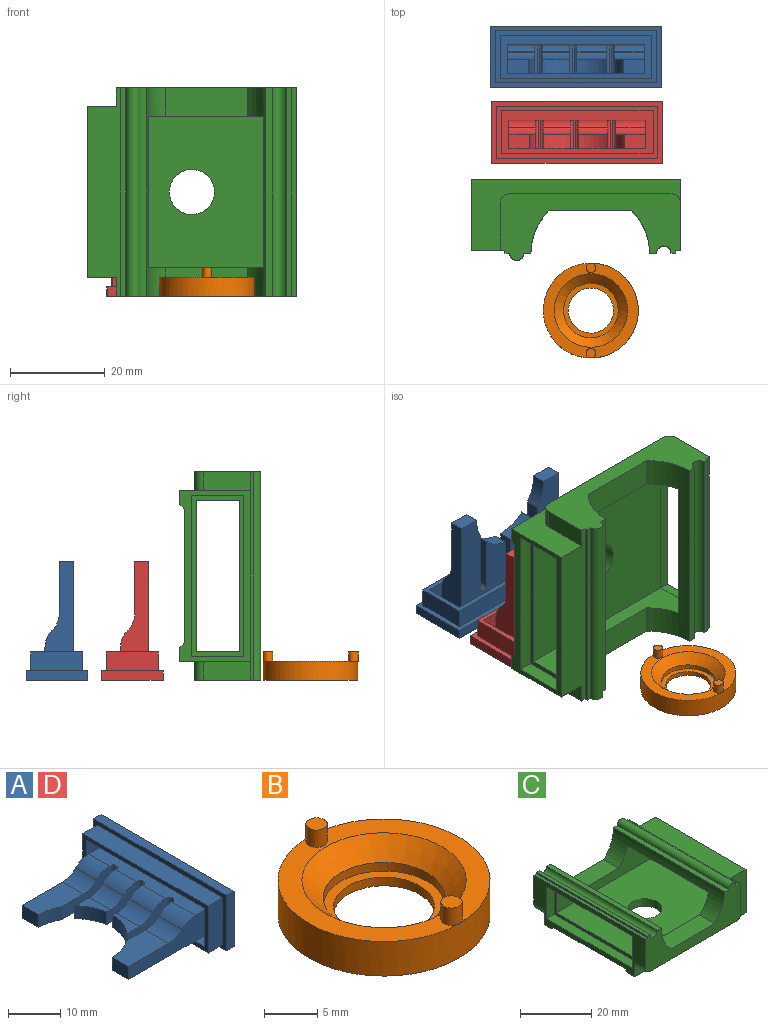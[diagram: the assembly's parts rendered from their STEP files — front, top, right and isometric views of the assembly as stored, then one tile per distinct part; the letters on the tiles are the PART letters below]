
ASSEMBLY  parts=4 mates=3
PART A: 57 faces, bbox 25x36x13 mm
  f0: plane 32x4mm, normal (0,0,-1), area 128mm2, adj f1,f7,f8,f24
  f1: plane 9x4mm, normal (0,-1,0), area 36mm2, adj f0,f2,f8,f24
  f2: plane 32x4mm, normal (0,0,1), area 128mm2, adj f1,f7,f8,f24
  f3: plane 11x4mm, normal (0,1,0), area 44mm2, adj f4,f6,f8,f41
  f4: plane 34x4mm, normal (0,0,1), area 136mm2, adj f3,f5,f8,f41
  f5: plane 11x4mm, normal (0,-1,0), area 44mm2, adj f4,f6,f8,f41
  f6: plane 34x4mm, normal (0,0,-1), area 136mm2, adj f3,f5,f8,f41
  f7: plane 9x4mm, normal (0,1,0), area 36mm2, adj f0,f2,f8,f24
  f8: plane 34x11mm, normal (-1,0,0), area 86mm2, adj f0,f1,f2,f3,f4,f5,f6,f7
  f9: plane 6x0.4mm, normal (-1,0,0), area 2.4mm2, adj f33,f37,f51,f52
  f10: plane 6x0.4mm, normal (-1,0,0), area 2.4mm2, adj f33,f37,f55,f56
  f11: plane 6x0.4mm, normal (-1,0,0), area 2.4mm2, adj f33,f37,f53,f54
  f12: cylinder r=5mm len=5.7mm, axis (0,-1,0), area 22.4mm2, adj f13,f33,f36,f38
  f13: plane 5.7x0.07mm, normal (-0.71,0,0.71), area 0.6mm2, adj f12,f36,f38,f47
  f14: cylinder r=10mm len=5.7mm, axis (0,0,-1), area 19.5mm2, adj f15,f32,f34,f37
  f15: plane 5.7x3.89mm, normal (0,0,1), area 11.8mm2, adj f14,f32,f34,f48
  f16: cylinder r=5mm len=6.3mm, axis (0,-1,0), area 24.7mm2, adj f17,f27,f28,f33
  f17: plane 6.3x0.07mm, normal (-0.71,0,0.71), area 0.6mm2, adj f16,f27,f28,f50
  f18: cylinder r=5mm len=6.3mm, axis (0,-1,0), area 24.7mm2, adj f19,f21,f22,f33
  f19: plane 6.3x0.07mm, normal (-0.71,0,0.71), area 0.6mm2, adj f18,f21,f22,f49
  f20: cylinder r=10mm len=6.3mm, axis (0,0,-1), area 20.6mm2, adj f21,f22,f23,f37
  f21: plane 8.4x6mm, normal (0,1,0), area 36.9mm2, adj f18,f19,f20,f23,f33,f37,f49,f53
  f22: plane 10.8x6mm, normal (0,-1,0), area 44.1mm2, adj f18,f19,f20,f23,f33,f37,f49,f56
  f23: plane 6.3x3.33mm, normal (0,0,1), area 10.8mm2, adj f20,f21,f22,f49
  f24: plane 32x9mm, normal (-1,0,0), area 115.2mm2, adj f0,f1,f2,f7,f27,f33,f36,f37
  f25: cylinder r=10mm len=5.86mm, axis (0,0,-1), area 18.8mm2, adj f26,f28,f29,f37
  f26: plane 4.4x3mm, normal (-1,0,0), area 13.2mm2, adj f25,f27,f29,f37
  f27: plane 23x6mm, normal (0,-1,0), area 94.5mm2, adj f16,f17,f24,f26,f29,f33,f37,f50
  f28: plane 12.54x6mm, normal (0,1,0), area 49.3mm2, adj f16,f17,f25,f29,f33,f37,f50,f55
  f29: plane 10.93x6.3mm, normal (0,0,1), area 61.3mm2, adj f25,f26,f27,f28,f50
  f30: cylinder r=5mm len=5.7mm, axis (0,-1,0), area 22.4mm2, adj f31,f32,f33,f34
  f31: plane 5.7x0.07mm, normal (-0.71,0,0.71), area 0.6mm2, adj f30,f32,f34,f48
  f32: plane 8.5x6mm, normal (0,-1,0), area 37.2mm2, adj f14,f15,f30,f31,f33,f37,f48,f54
  f33: plane 28.8x4.93mm, normal (0,0,1), area 138mm2, adj f9,f10,f11,f12,f16,f18,f21,f22
  f34: plane 11.36x6mm, normal (0,1,0), area 45.8mm2, adj f14,f15,f30,f31,f33,f37,f48,f51
  f35: cylinder r=10mm len=4.93mm, axis (0,0,-1), area 15.5mm2, adj f37,f38,f39,f40
  f36: plane 23x6mm, normal (0,1,0), area 94.5mm2, adj f12,f13,f24,f33,f37,f39,f40,f47
  f37: plane 28.8x23mm, normal (0,0,-1), area 451.2mm2, adj f9,f10,f11,f14,f20,f21,f22,f24
  f38: plane 13.47x6mm, normal (0,-1,0), area 52.1mm2, adj f12,f13,f33,f35,f37,f40,f47,f52
  f39: plane 4.4x3mm, normal (-1,0,0), area 13.2mm2, adj f35,f36,f37,f40
  f40: plane 10.93x5.7mm, normal (0,0,1), area 58mm2, adj f35,f36,f38,f39,f47
  f41: plane 36x13mm, normal (-1,0,0), area 94mm2, adj f3,f4,f5,f6,f42,f43,f44,f45
  f42: plane 36x2mm, normal (0,0,-1), area 72mm2, adj f41,f43,f45,f46
  f43: plane 13x2mm, normal (0,1,0), area 26mm2, adj f41,f42,f44,f46
  f44: plane 36x2mm, normal (0,0,1), area 72mm2, adj f41,f43,f45,f46
  f45: plane 13x2mm, normal (0,-1,0), area 26mm2, adj f41,f42,f44,f46
  f46: plane 36x13mm, normal (1,0,0), area 468mm2, adj f42,f43,f44,f45
  f47: cylinder r=5mm len=5.7mm, axis (0,1,0), area 22.4mm2, adj f13,f36,f38,f40
  f48: cylinder r=5mm len=5.7mm, axis (0,1,0), area 22.4mm2, adj f15,f31,f32,f34
  f49: cylinder r=5mm len=6.3mm, axis (0,1,0), area 24.7mm2, adj f19,f21,f22,f23
  f50: cylinder r=5mm len=6.3mm, axis (0,1,0), area 24.7mm2, adj f17,f27,f28,f29
  f51: cylinder r=0.6mm len=6mm, axis (0,0,1), area 5.7mm2, adj f9,f33,f34,f37
  f52: cylinder r=0.6mm len=6mm, axis (0,0,-1), area 5.7mm2, adj f9,f33,f37,f38
  f53: cylinder r=0.6mm len=6mm, axis (0,0,1), area 5.7mm2, adj f11,f21,f33,f37
  f54: cylinder r=0.6mm len=6mm, axis (0,0,-1), area 5.7mm2, adj f11,f32,f33,f37
  f55: cylinder r=0.6mm len=6mm, axis (0,0,1), area 5.7mm2, adj f10,f28,f33,f37
  f56: cylinder r=0.6mm len=6mm, axis (0,0,-1), area 5.7mm2, adj f10,f22,f33,f37
PART B: 11 faces, bbox 20x20x6 mm
  f0: cylinder r=5.75mm len=11.5mm, axis (0,0,-1), area 36.1mm2, adj f5,f6
  f1: cylinder r=10mm len=20mm, axis (0,0,-1), area 251.3mm2, adj f2,f3
  f2: plane 20x20mm, normal (0,0,1), area 119.2mm2, adj f1,f6,f7,f9
  f3: plane 20x20mm, normal (0,0,-1), area 243.3mm2, adj f1,f4
  f4: cylinder r=4.75mm len=9.5mm, axis (0,0,-1), area 29.8mm2, adj f3,f5
  f5: plane 11.5x11.5mm, normal (0,0,1), area 33mm2, adj f0,f4
  f6: cone r=5.75mm half-angle=45deg, axis (0,0,1), area 120mm2, adj f0,f2
  f7: cylinder r=1mm len=2mm, axis (0,0,-1), area 12.6mm2, adj f2,f8
  f8: plane 2x2mm, normal (0,0,1), area 3.1mm2, adj f7
  f9: cylinder r=1mm len=2mm, axis (0,0,-1), area 12.6mm2, adj f2,f10
  f10: plane 2x2mm, normal (0,0,1), area 3.1mm2, adj f9
PART C: 49 faces, bbox 44x44x17 mm
  f0: plane 38x14mm, normal (0,1,0), area 268.4mm2, adj f3,f5,f11,f12,f13,f17,f18,f19
  f1: plane 38x14mm, normal (0,-1,0), area 268.4mm2, adj f3,f4,f5,f11,f12,f16,f17,f18
  f2: plane 36x14.9mm, normal (1,0,0), area 136.3mm2, adj f3,f15,f26,f27,f28,f29,f30,f31
  f3: plane 44x7mm, normal (0,0,1), area 260mm2, adj f0,f1,f2,f22,f26,f28,f43,f44
  f4: plane 34x4mm, normal (0,0,-1), area 136mm2, adj f1,f28,f46,f48
  f5: plane 44x14.9mm, normal (-1,0,0), area 215.5mm2, adj f0,f1,f15,f21,f26,f27,f28,f29
  f6: plane 38x9mm, normal (0,1,0), area 212.6mm2, adj f8,f9,f10,f11,f12,f16,f34,f39
  f7: plane 38x9mm, normal (0,-1,0), area 212.6mm2, adj f8,f9,f10,f11,f12,f13,f34,f39
  f8: plane 38x32mm, normal (0,0,1), area 1145.1mm2, adj f6,f7,f14,f34,f39
  f9: plane 32x3.87mm, normal (0,0,-1), area 123.7mm2, adj f6,f7,f12,f39
  f10: plane 32x9.87mm, normal (0,0,-1), area 315.7mm2, adj f6,f7,f11,f34
  f11: cylinder r=12.5mm len=44mm, axis (0,1,0), area 217.5mm2, adj f0,f1,f6,f7,f10,f13,f16,f25
  f12: cylinder r=12.5mm len=44mm, axis (0,1,0), area 217.5mm2, adj f0,f1,f6,f7,f9,f13,f16,f17
  f13: plane 17.35x6mm, normal (0,0,1), area 104.1mm2, adj f0,f7,f11,f12
  f14: cylinder r=4.75mm len=9.5mm, axis (0,0,1), area 77.7mm2, adj f8,f15
  f15: plane 44x28.21mm, normal (0,0,-1), area 1170.2mm2, adj f2,f5,f14,f41,f42
  f16: plane 17.35x6mm, normal (0,0,1), area 104.1mm2, adj f1,f6,f11,f12
  f17: plane 44x1.5mm, normal (0,0,1), area 66mm2, adj f0,f1,f12,f18
  f18: cylinder r=1.5mm len=44mm, axis (0,1,0), area 207.3mm2, adj f0,f1,f17,f19
  f19: plane 44x1mm, normal (0,0,1), area 44mm2, adj f0,f1,f18,f20
  f20: plane 44x0.6mm, normal (-1,0,0), area 26.4mm2, adj f0,f1,f19,f21
  f21: plane 44x1mm, normal (0,0,1), area 44mm2, adj f0,f1,f5,f20
  f22: plane 44x0.6mm, normal (1,0,0), area 26.4mm2, adj f0,f1,f3,f23
  f23: plane 44x1mm, normal (0,0,1), area 44mm2, adj f0,f1,f22,f24
  f24: cylinder r=1.5mm len=44mm, axis (0,1,0), area 207.3mm2, adj f0,f1,f23,f25
  f25: plane 44x1.5mm, normal (0,0,1), area 66mm2, adj f0,f1,f11,f24
  f26: plane 44x14.9mm, normal (0,1,0), area 205.1mm2, adj f2,f3,f5,f27,f40,f44,f45,f47
  f27: plane 44x3mm, normal (0,0,-1), area 132mm2, adj f2,f5,f26,f42
  f28: plane 44x14.9mm, normal (0,-1,0), area 205.1mm2, adj f2,f3,f4,f5,f29,f43,f46,f48
  f29: plane 44x3mm, normal (0,0,-1), area 132mm2, adj f2,f5,f28,f41
  f30: plane 11x3mm, normal (0,1,0), area 33mm2, adj f2,f31,f33,f34
  f31: plane 34x3mm, normal (0,0,1), area 102mm2, adj f2,f30,f32,f34
  f32: plane 11x3mm, normal (0,-1,0), area 33mm2, adj f2,f31,f33,f34
  f33: plane 34x3mm, normal (0,0,-1), area 102mm2, adj f2,f30,f32,f34
  f34: plane 34x11mm, normal (1,0,0), area 86mm2, adj f6,f7,f8,f10,f30,f31,f32,f33
  f35: plane 11x3mm, normal (0,-1,0), area 33mm2, adj f5,f36,f38,f39
  f36: plane 34x3mm, normal (0,0,1), area 102mm2, adj f5,f35,f37,f39
  f37: plane 11x3mm, normal (0,1,0), area 33mm2, adj f5,f36,f38,f39
  f38: plane 34x3mm, normal (0,0,-1), area 102mm2, adj f5,f35,f37,f39
  f39: plane 34x11mm, normal (-1,0,0), area 86mm2, adj f6,f7,f8,f9,f35,f36,f37,f38
  f40: plane 34x4mm, normal (0,0,-1), area 136mm2, adj f0,f26,f45,f47
  f41: plane 44x0.9mm, normal (0,0.71,-0.71), area 55.8mm2, adj f2,f5,f15,f29
  f42: plane 44x0.9mm, normal (0,-0.71,-0.71), area 55.8mm2, adj f2,f5,f15,f27
  f43: plane 9.9x4mm, normal (1,0,0), area 39.6mm2, adj f1,f3,f28,f46
  f44: plane 9.9x4mm, normal (1,0,0), area 39.6mm2, adj f0,f3,f26,f45
  f45: cylinder r=2mm len=4mm, axis (0,-1,0), area 12.6mm2, adj f0,f26,f40,f44
  f46: cylinder r=2mm len=4mm, axis (0,-1,0), area 12.6mm2, adj f1,f4,f28,f43
  f47: cylinder r=2mm len=4mm, axis (0,-1,0), area 12.6mm2, adj f0,f5,f26,f40
  f48: cylinder r=2mm len=4mm, axis (0,-1,0), area 12.6mm2, adj f1,f4,f5,f28
PART D: same geometry as A
PLACE A rot(axis=(-0.58,0.58,0.58),120deg) t=(21.98,5.73,27.98)mm
PLACE B t=(25.12,-44.24,-0.02)mm
PLACE C rot(axis=(0,0.71,-0.71),180deg) t=(24.98,-32.21,21.98)mm fixed
PLACE D rot(axis=(-0.58,0.58,0.58),120deg) t=(22.23,-10.17,27.98)mm
MATE planar D.f46 <-> C.f0  axis (0,0,-1) through (22.23,-6.67,-0.02)mm
MATE planar C.f0 <-> A.f46  axis (0,0,-1) through (24.98,-23.21,-0.02)mm
MATE planar C.f0 <-> B.f4  axis (0,0,-1) through (24.58,-24.47,-0.02)mm
